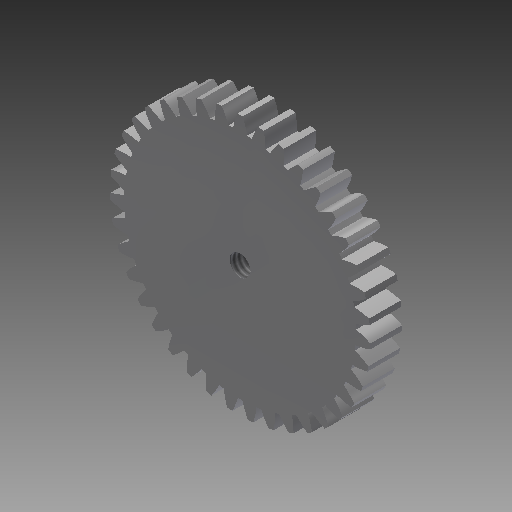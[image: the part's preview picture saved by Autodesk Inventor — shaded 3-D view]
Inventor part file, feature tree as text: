
AUTODESK INVENTOR PART (.ipt)
format: ipt  version: 2017 (Build 210142000, 142)  size: 306,688 bytes
history: native  units: mm (DEFAULTED — no unit token found)
features: plane x3, other x3, sketch x3, extrude x1, hole x1
ambient origin geometry x8: Origin, YZ Plane, XZ Plane, XY Plane, X Axis, Y Axis, Z Axis, Center Point
bodies: Solid1 (feature_tree)
feature tree (11):
  extrude  "Extrusion1"  Depth=5.0mm TaperAngle=0.0deg
  plane  "Work Plane2"
  plane  "Work Plane8"
  plane  "Work Plane9"
  other  "Spur Gear"
  hole  "Hole1"  [1 undecoded]
  sketch  "Sketch1"  dims[d0=41.0mm d1=5.0mm d2=0.0mm]
  sketch  "Sketch2"  dims[d3=39.0mm d4=10.0mm d5=0.0mm]
  other  "Srf1"
  sketch  "Sketch4"  dims[d16=43.5mm d17=0.0mm d34=0.805537mm d39=0.0mm d41=0.0mm d43=43.5mm d46=43.5mm d47=0.0mm d48=0.0mm d49=3.302mm d50=8.331mm d51=4.0mm d52=2.0mm d53=90.0deg d54=12.3mm d55=20.594885mm]
  other  "Pitch Diameter"
note: 1 required parameter value undecoded (feature->parameter linkage not recoverable at this tier; creation-order binding heuristic only, values carry confidence <= 0.55)
